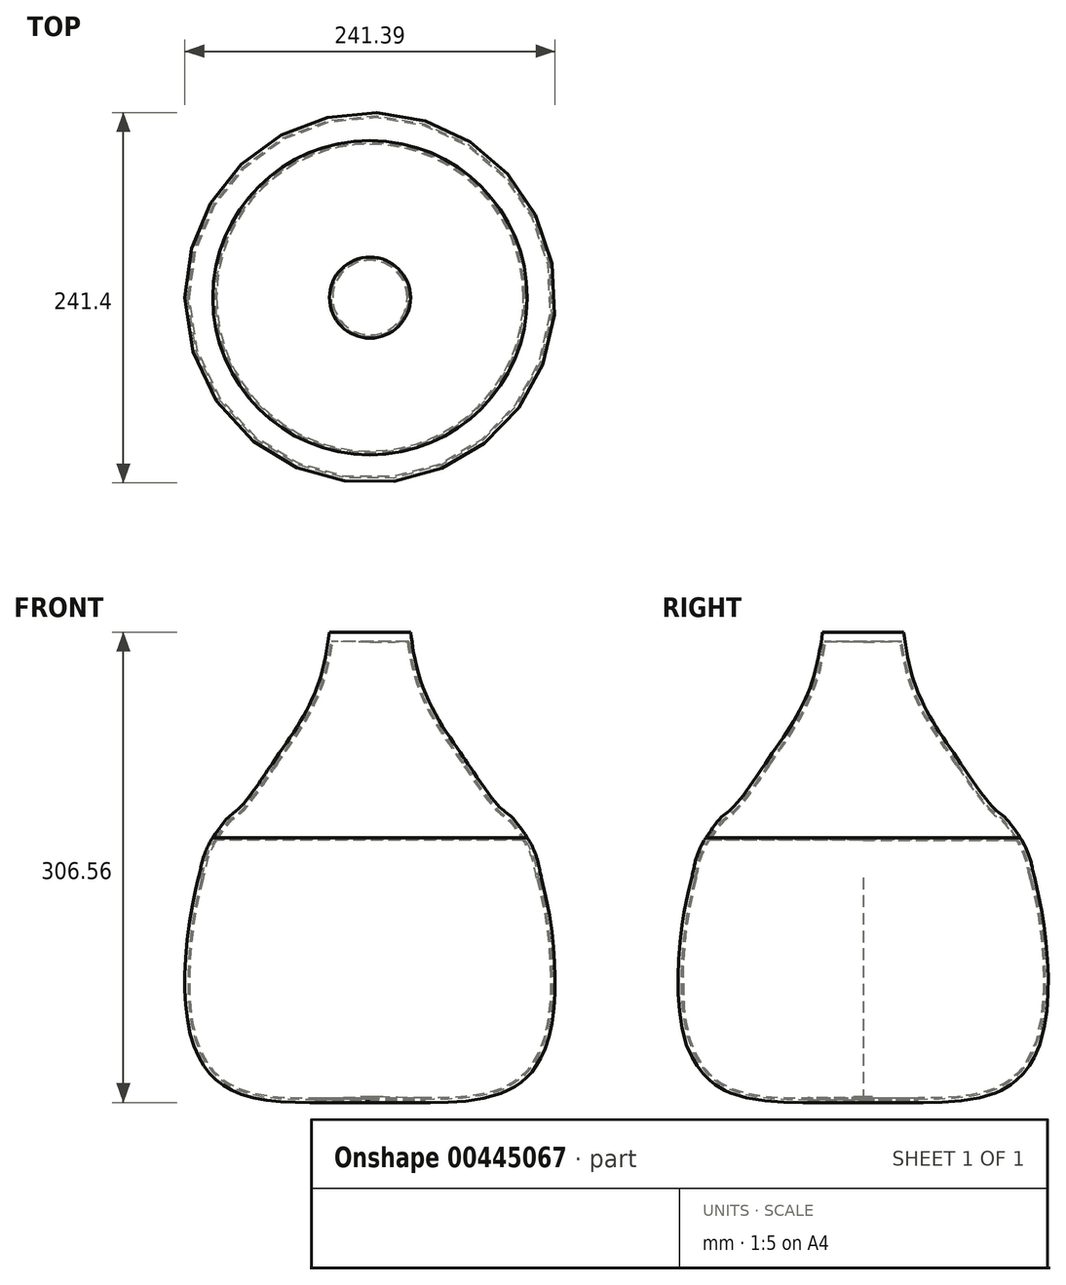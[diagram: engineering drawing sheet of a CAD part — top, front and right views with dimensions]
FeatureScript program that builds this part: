
annotation { "Feature Type Name" : "Feature", "Feature Type Description" : "" }
export const myFeature = defineFeature(function(context is Context, id is Id, definition is map)
    precondition{}
    {
        {
            var Q0;
            Q0=qCreatedBy(makeId("Front.planeOp"),FACE);
            var sketch = newSketch(context, id + "F0", { "sketchPlane" : qUnion([Q0])});
            skLineSegment(sketch, "E0", {"start": v(0, 134.33) * mm, "end": v(0, -170.47) * mm});
            skLineSegment(sketch, "E1.bottom", {"start": v(0, 134.33) * mm, "end": v(-25.4, 134.59) * mm});
            skLineSegment(sketch, "E1.left", {"start": v(0, 134.33) * mm, "end": v(0, 132.7) * mm});
            skLineSegment(sketch, "E1.right", {"start": v(-25.4, 134.59) * mm, "end": v(-25.4, 134.33) * mm});
            skFitSpline(sketch, "E2", {"points": [v(-25.4, 134.59) * mm, v(-62.87, 48.5) * mm], "startDerivative": vector(-20.05, -129.06) * mm, "endDerivative": vector(-54.15, -80.74) * mm});
            skFitSpline(sketch, "E3", {"points": [v(-62.87, 48.5) * mm, v(-101.65, 0) * mm], "startDerivative": vector(-97.56, -145.48) * mm, "endDerivative": vector(-58.64, -87.43) * mm});
            skFitSpline(sketch, "E4", {"points": [v(-101.65, 0) * mm, v(-110.78, -25.7) * mm], "startDerivative": vector(-15.17, -22.62) * mm, "endDerivative": vector(-6.2, -26.53) * mm});
            skFitSpline(sketch, "E5", {"points": [v(-110.78, -25.7) * mm, v(-101.65, -154.53) * mm, v(0, -170.47) * mm], "startDerivative": vector(-68.5, -292.74) * mm, "endDerivative": vector(262.29, 0) * mm});
            skFitSpline(sketch, "E6.0", {"points": [v(-24.41, 134.43) * mm, v(-26.09, 123.64) * mm, v(-30.2, 105.4) * mm, v(-38.62, 84.55) * mm, v(-49.17, 66.78) * mm, v(-57.53, 54.66) * mm, v(-62.04, 47.94) * mm]});
            skFitSpline(sketch, "E7.0", {"points": [v(-62.04, 47.94) * mm, v(-66.11, 41.87) * mm, v(-72.82, 32.16) * mm, v(-78.4, 24.74) * mm, v(-81.67, 20.83) * mm, v(-83.63, 18.72) * mm, v(-85.22, 17.22) * mm, v(-86.55, 16.15) * mm, v(-87.7, 15.34) * mm, v(-88.76, 14.6) * mm, v(-89.85, 13.7) * mm, v(-91.14, 12.46) * mm, v(-92.76, 10.63) * mm, v(-95.5, 7.15) * mm, v(-98.39, 3.08) * mm, v(-100.82, -0.56) * mm]});
            skFitSpline(sketch, "E8.0", {"points": [v(-100.82, -0.56) * mm, v(-102.05, -2.39) * mm, v(-104.15, -6.28) * mm, v(-107.25, -14.73) * mm, v(-108.77, -21.5) * mm, v(-109.8, -25.93) * mm]});
            skFitSpline(sketch, "E9.0", {"points": [v(-109.8, -25.93) * mm, v(-112.66, -38.1) * mm, v(-116.06, -56.58) * mm, v(-118.29, -80.3) * mm, v(-118.67, -97.3) * mm, v(-117.63, -113.16) * mm, v(-115.03, -127.52) * mm, v(-111.46, -137.95) * mm, v(-107.7, -145.2) * mm, v(-104.42, -150.06) * mm, v(-100.66, -154.3) * mm, v(-96.4, -157.89) * mm, v(-91.67, -160.9) * mm, v(-84.75, -164.2) * mm, v(-75.03, -167.13) * mm, v(-61.9, -169.09) * mm, v(-47.57, -169.89) * mm, v(-27.22, -169.94) * mm, v(-10.95, -169.47) * mm, v(0, -169.47) * mm]});
            skLineSegment(sketch, "E10.0", {"start": v(0, 128.26) * mm, "end": v(-25.4, 128.5) * mm});
            skFitSpline(sketch, "E11.0", {"points": [v(-63.7, 49.04) * mm, v(-67.76, 42.99) * mm, v(-74.44, 33.3) * mm, v(-79.98, 25.96) * mm, v(-83.17, 22.14) * mm, v(-85.05, 20.11) * mm, v(-86.54, 18.72) * mm, v(-87.75, 17.75) * mm, v(-88.83, 16.98) * mm, v(-89.95, 16.19) * mm, v(-91.18, 15.2) * mm, v(-92.6, 13.83) * mm, v(-94.3, 11.9) * mm, v(-97.12, 8.32) * mm, v(-100.03, 4.2) * mm, v(-102.48, 0.55) * mm]});
            skFitSpline(sketch, "E12.0", {"points": [v(-102.48, 0.55) * mm, v(-103.78, -1.39) * mm, v(-105.98, -5.48) * mm, v(-109.18, -14.22) * mm, v(-110.71, -21.07) * mm, v(-111.75, -25.48) * mm]});
            skFitSpline(sketch, "E13.0", {"points": [v(-26.38, 134.74) * mm, v(-28.04, 124.02) * mm, v(-32.12, 105.96) * mm, v(-40.4, 85.44) * mm, v(-50.82, 67.89) * mm, v(-59.18, 55.78) * mm, v(-63.7, 49.04) * mm]});
            skFitSpline(sketch, "E14.0", {"points": [v(-111.75, -25.48) * mm, v(-114.6, -37.7) * mm, v(-118.03, -56.29) * mm, v(-120.28, -80.19) * mm, v(-120.67, -97.34) * mm, v(-119.61, -113.39) * mm, v(-116.97, -128) * mm, v(-113.3, -138.7) * mm, v(-109.42, -146.22) * mm, v(-106, -151.28) * mm, v(-102.06, -155.73) * mm, v(-97.59, -159.5) * mm, v(-92.63, -162.65) * mm, v(-85.44, -166.08) * mm, v(-75.44, -169.09) * mm, v(-62.08, -171.07) * mm, v(-47.61, -171.88) * mm, v(-32.28, -171.92) * mm, v(-16.33, -171.62) * mm, v(-5.45, -171.46) * mm, v(0, -171.46) * mm]});
            skLineSegment(sketch, "E15.0", {"start": v(-0.02, 140.68) * mm, "end": v(-25.26, 140.93) * mm});
            skLineSegment(sketch, "E16", {"start": v(-25.4, 134.59) * mm, "end": v(-26.4, 134.59) * mm});
            skFitSpline(sketch, "E17.0", {"points": [v(-108.84, -26.16) * mm, v(-111.68, -38.3) * mm, v(-115.08, -56.73) * mm, v(-117.3, -80.37) * mm, v(-117.68, -97.29) * mm, v(-116.64, -113.04) * mm, v(-114.06, -127.28) * mm, v(-110.53, -137.57) * mm, v(-106.84, -144.7) * mm, v(-103.63, -149.46) * mm, v(-99.97, -153.59) * mm, v(-95.82, -157.08) * mm, v(-91.2, -160.03) * mm, v(-84.4, -163.27) * mm, v(-74.83, -166.16) * mm, v(-61.8, -168.1) * mm, v(-47.54, -168.9) * mm, v(-27.24, -168.95) * mm, v(-10.97, -168.48) * mm, v(0, -168.48) * mm]});
            skFitSpline(sketch, "E18.0", {"points": [v(-100, -1.1) * mm, v(-101.2, -2.89) * mm, v(-103.24, -6.68) * mm, v(-106.3, -14.99) * mm, v(-107.8, -21.73) * mm, v(-108.84, -26.16) * mm]});
            skFitSpline(sketch, "E19.0", {"points": [v(-61.22, 47.38) * mm, v(-65.3, 41.31) * mm, v(-72.01, 31.58) * mm, v(-77.62, 24.13) * mm, v(-80.92, 20.18) * mm, v(-82.92, 18.03) * mm, v(-84.57, 16.48) * mm, v(-85.96, 15.36) * mm, v(-87.14, 14.52) * mm, v(-88.16, 13.8) * mm, v(-89.19, 12.97) * mm, v(-90.42, 11.78) * mm, v(-92, 10) * mm, v(-94.7, 6.57) * mm, v(-97.57, 2.51) * mm, v(-100, -1.1) * mm]});
            skFitSpline(sketch, "E20.0", {"points": [v(-23.43, 134.28) * mm, v(-25.11, 123.45) * mm, v(-29.25, 105.11) * mm, v(-37.73, 84.1) * mm, v(-48.34, 66.23) * mm, v(-56.72, 54.1) * mm, v(-61.22, 47.38) * mm]});
            skLineSegment(sketch, "E21", {"start": v(0, -170.47) * mm, "end": v(0, -171.46) * mm});
            skSolve(sketch);
        }
        {
            var Q0;
            Q0=makeQuery(id+"F0.imprint","IMPRINT",FACE,{"disambiguationData":[TD([[makeQuery(id+"F0.imprint","IMPRINT",EDGE,{"derivedFrom":sQuery(id+"F0.wireOp",EDGE,"E2")}),-1.0]])]});
            var Q1;
            Q1=makeQuery(id+"F0.imprint","IMPRINT",FACE,{"disambiguationData":[TD([[makeQuery(id+"F0.imprint","IMPRINT",EDGE,{"derivedFrom":sQuery(id+"F0.wireOp",EDGE,"E1.bottom")}),1.0]])]});
            var Q2;
            Q2=sQuery(id+"F0.wireOp",EDGE,"E0");
            revolve(context, id + "F1", {"entities" : qUnion([Q0, Q1]), "axis" : qUnion([Q2]), "revolveType" : RevolveType.FULL});
        }
        {
            var Q0;
            {var subQ0=sQuery(id+"F0.wireOp",EDGE,"E6.0");Q0=makeQuery(id+"F0.imprint","IMPRINT",FACE,{"disambiguationData":[TD([[makeQuery(id+"F0.imprint","IMPRINT",EDGE,{"derivedFrom":subQ0}),1.0]])]});}
            var Q1;
            Q1=sQuery(id+"F0.wireOp",EDGE,"E0");
            revolve(context, id + "F2", {"entities" : qUnion([Q0]), "axis" : qUnion([Q1]), "revolveType" : RevolveType.FULL});
        }
        {
            var Q0;
            Q0=makeQuery(id+"F1.opRevolve","SWEPT_FACE",FACE,{"disambiguationData":[OSD([sQuery(id+"F0.wireOp",EDGE,"E16")])]});
            var sketch = newSketch(context, id + "F3", { "sketchPlane" : qUnion([Q0])});
            skCircle(sketch, "E22", {"center": v(0, 0) * mm, "radius": 24.48 * mm});
            skSolve(sketch);
        }
        {
            var Q0;
            Q0=sQuery(id+"F3.wireOp",EDGE,"E22");
            extrude(context, id + "F4", {"bodyType" : ToolBodyType.SURFACE, "surfaceEntities" : qUnion([Q0]), "oppositeDirection" : true, "depth" : 304.8 * mm, "offsetDistance" : 25.4 * mm});
        }
    });
